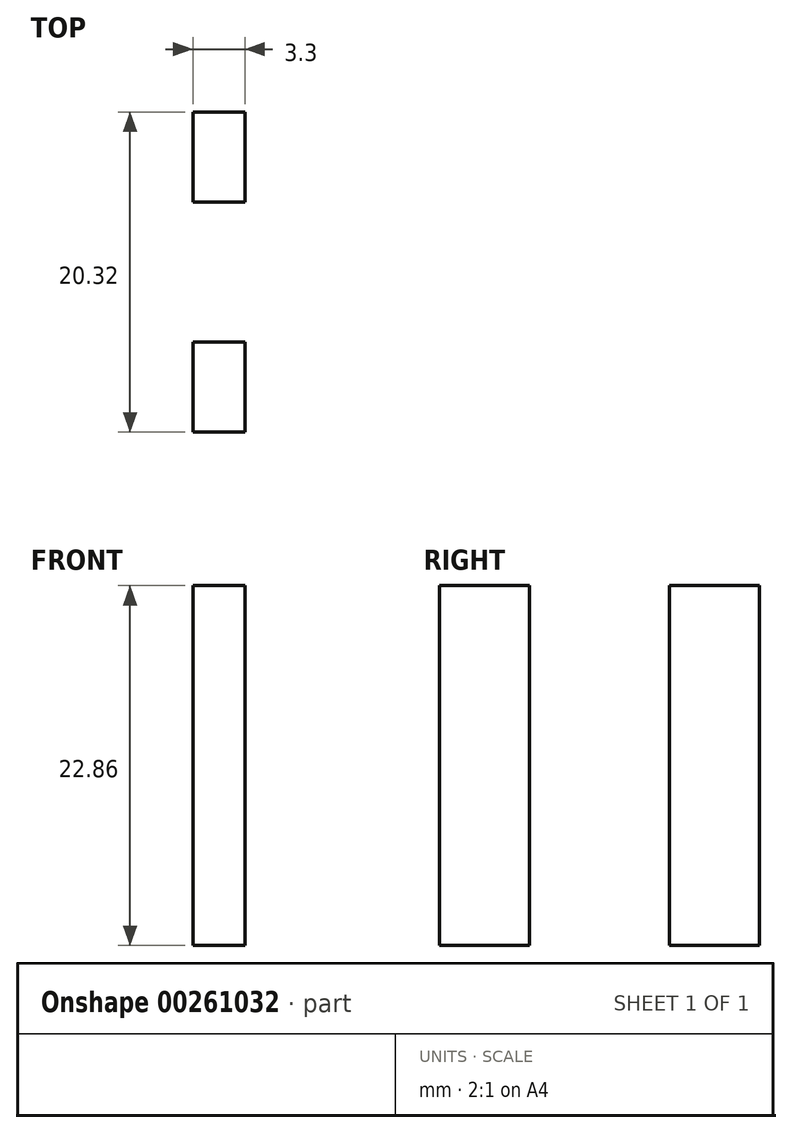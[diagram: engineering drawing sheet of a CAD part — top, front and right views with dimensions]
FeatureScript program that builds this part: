
annotation { "Feature Type Name" : "Feature", "Feature Type Description" : "" }
export const myFeature = defineFeature(function(context is Context, id is Id, definition is map)
    precondition{}
    {
        {
            var Q0;
            Q0=qCreatedBy(makeId("Right.planeOp"),FACE);
            var sketch = newSketch(context, id + "F0", { "sketchPlane" : qUnion([Q0])});
            skLineSegment(sketch, "E0.bottom", {"start": v(10.16, 11.43) * mm, "end": v(4.45, 11.43) * mm});
            skLineSegment(sketch, "E0.top", {"start": v(10.16, -11.43) * mm, "end": v(4.45, -11.43) * mm});
            skLineSegment(sketch, "E0.left", {"start": v(10.16, 11.43) * mm, "end": v(10.16, -11.43) * mm});
            skLineSegment(sketch, "E0.right", {"start": v(-10.16, 11.43) * mm, "end": v(-10.16, -11.43) * mm});
            skPoint(sketch, "E0.middle", {"position": v(0, 0) * mm});
            skLineSegment(sketch, "E1", {"start": v(-4.45, 11.43) * mm, "end": v(-4.44, -11.43) * mm});
            skLineSegment(sketch, "E2.MirrorCS", {"start": v(4.44, 11.43) * mm, "end": v(4.45, -11.43) * mm});
            skLineSegment(sketch, "E3.trimOffspring", {"start": v(-4.45, 11.43) * mm, "end": v(-10.16, 11.43) * mm});
            skLineSegment(sketch, "E4.trimOffspring", {"start": v(-4.45, -11.43) * mm, "end": v(-10.16, -11.43) * mm});
            skSolve(sketch);
        }
        {
            var Q0;
            Q0 = qSketchRegion(id + "F0", true);
            extrude(context, id + "F1", {"entities" : qUnion([Q0]), "depth" : 3.3 * mm});
        }
    });
